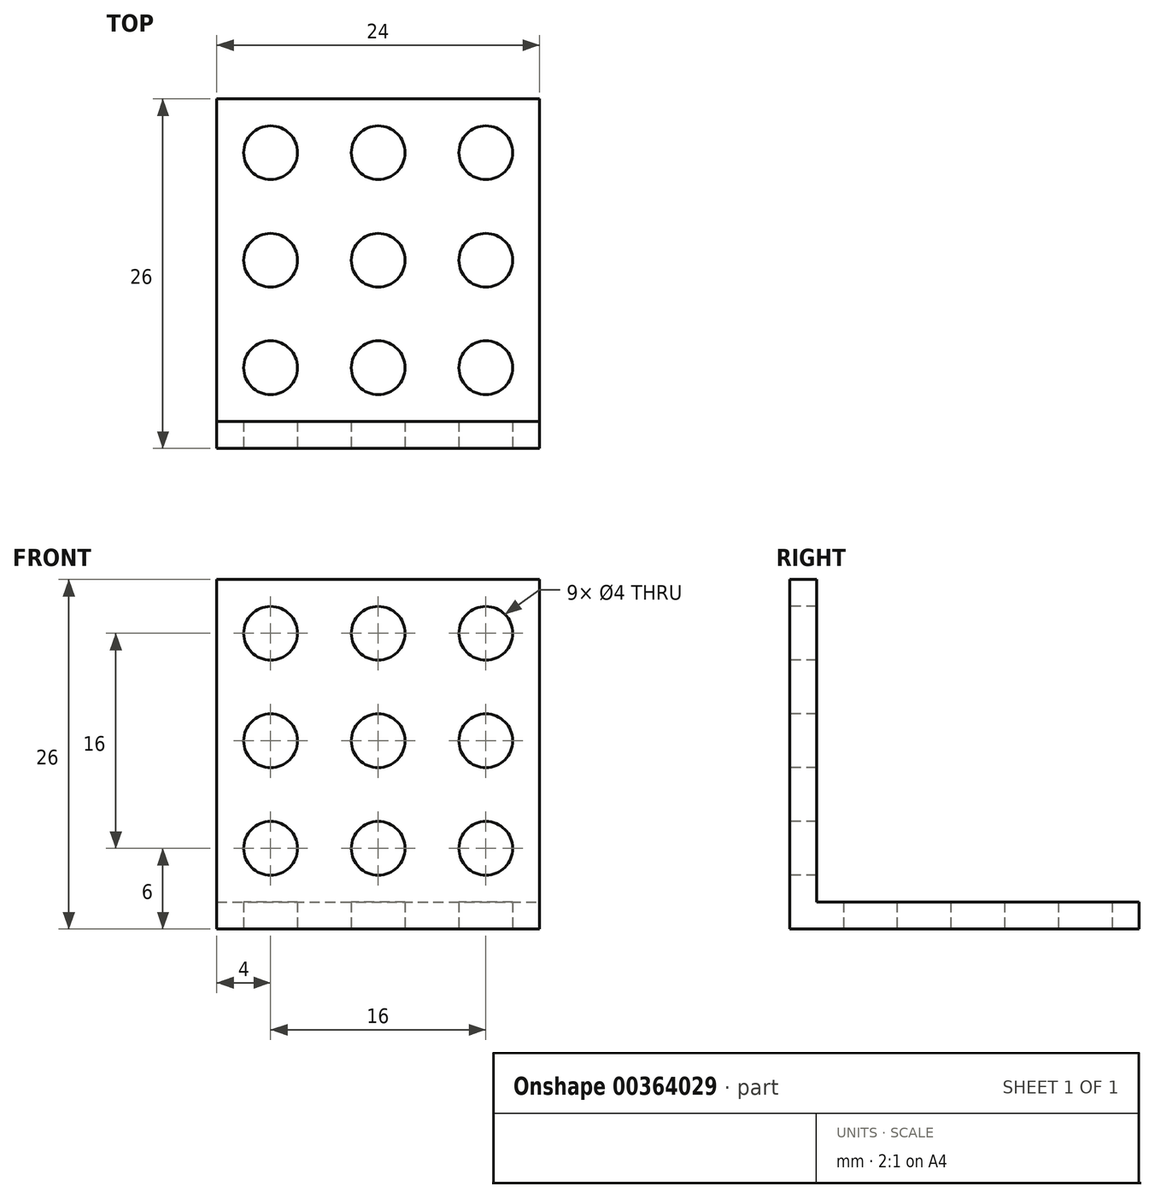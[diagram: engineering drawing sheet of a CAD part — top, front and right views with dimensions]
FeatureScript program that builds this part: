
annotation { "Feature Type Name" : "Feature", "Feature Type Description" : "" }
export const myFeature = defineFeature(function(context is Context, id is Id, definition is map)
    precondition{}
    {
        {
            var Q0;
            Q0=qCreatedBy(makeId("Top.planeOp"),FACE);
            var sketch = newSketch(context, id + "F0", { "sketchPlane" : qUnion([Q0])});
            skLineSegment(sketch, "E0", {"start": v(0, 0) * mm, "end": v(12, 0) * mm});
            skLineSegment(sketch, "E1", {"start": v(12, 0) * mm, "end": v(12, -26) * mm});
            skLineSegment(sketch, "E2", {"start": v(12, -26) * mm, "end": v(-12, -26) * mm});
            skLineSegment(sketch, "E3", {"start": v(-12, -26) * mm, "end": v(-12, 0) * mm});
            skLineSegment(sketch, "E4", {"start": v(-12, 0) * mm, "end": v(0, 0) * mm});
            skLineSegment(sketch, "E5", {"start": v(-12, -4) * mm, "end": v(-8, -4) * mm, "construction": true});
            skCircle(sketch, "E6", {"center": v(-8, -4) * mm, "radius": 2 * mm});
            skCircle(sketch, "E7.0.1.0", {"center": v(-8, -12) * mm, "radius": 2 * mm});
            skCircle(sketch, "E7.0.2.0", {"center": v(-8, -20) * mm, "radius": 2 * mm});
            skCircle(sketch, "E7.1.0.0", {"center": v(0, -4) * mm, "radius": 2 * mm});
            skCircle(sketch, "E7.1.1.0", {"center": v(0, -12) * mm, "radius": 2 * mm});
            skCircle(sketch, "E7.1.2.0", {"center": v(0, -20) * mm, "radius": 2 * mm});
            skCircle(sketch, "E7.2.0.0", {"center": v(8, -4) * mm, "radius": 2 * mm});
            skCircle(sketch, "E7.2.1.0", {"center": v(8, -12) * mm, "radius": 2 * mm});
            skCircle(sketch, "E7.2.2.0", {"center": v(8, -20) * mm, "radius": 2 * mm});
            skLineSegment(sketch, "E7.direction1", {"start": v(-8, -4) * mm, "end": v(0, -4) * mm, "construction": true});
            skLineSegment(sketch, "E7.direction2", {"start": v(-8, -4) * mm, "end": v(-8, -12) * mm, "construction": true});
            skSolve(sketch);
        }
        {
            var Q0;
            Q0 = qSketchRegion(id + "F0", true);
            extrude(context, id + "F1", {"entities" : qUnion([Q0]), "depth" : 2 * mm});
        }
        {
            var Q0;
            Q0=makeQuery(id+"F1.opExtrude","CAP_FACE",FACE,{"disambiguationData":[OSD([sQuery(id+"F0.wireOp",EDGE,"E0"),sQuery(id+"F0.wireOp",EDGE,"E1"),sQuery(id+"F0.wireOp",EDGE,"E2"),sQuery(id+"F0.wireOp",EDGE,"E3"),sQuery(id+"F0.wireOp",EDGE,"E4"),sQuery(id+"F0.wireOp",EDGE,"E6"),sQuery(id+"F0.wireOp",EDGE,"E7.0.1.0"),sQuery(id+"F0.wireOp",EDGE,"E7.0.2.0"),sQuery(id+"F0.wireOp",EDGE,"E7.1.0.0"),sQuery(id+"F0.wireOp",EDGE,"E7.1.1.0"),sQuery(id+"F0.wireOp",EDGE,"E7.1.2.0"),sQuery(id+"F0.wireOp",EDGE,"E7.2.0.0"),sQuery(id+"F0.wireOp",EDGE,"E7.2.1.0"),sQuery(id+"F0.wireOp",EDGE,"E7.2.2.0")])],"isStart":false});
            var sketch = newSketch(context, id + "F2", { "sketchPlane" : qUnion([Q0])});
            skLineSegment(sketch, "E8.bottom", {"start": v(-12, -26) * mm, "end": v(12, -26) * mm});
            skLineSegment(sketch, "E8.top", {"start": v(-12, -24) * mm, "end": v(12, -24) * mm});
            skLineSegment(sketch, "E8.left", {"start": v(-12, -26) * mm, "end": v(-12, -24) * mm});
            skLineSegment(sketch, "E8.right", {"start": v(12, -26) * mm, "end": v(12, -24) * mm});
            skSolve(sketch);
        }
        {
            var Q0;
            Q0 = qSketchRegion(id + "F2", true);
            extrude(context, id + "F3", {"entities" : qUnion([Q0]), "operationType" : NewBodyOperationType.ADD, "depth" : 24 * mm});
        }
        {
            var Q0;
            Q0=makeQuery(id+"F3.boolean.opBoolean","MERGE",FACE,{"derivedFrom":[makeQuery(id+"F1.opExtrude","SWEPT_FACE",FACE,{"disambiguationData":[OSD([sQuery(id+"F0.wireOp",EDGE,"E2")])]}),makeQuery(id+"F3.opExtrude","SWEPT_FACE",FACE,{"disambiguationData":[OSD([sQuery(id+"F2.wireOp",EDGE,"E8.bottom")])]})]});
            var sketch = newSketch(context, id + "F4", { "sketchPlane" : qUnion([Q0])});
            skLineSegment(sketch, "E9", {"start": v(-12, 22) * mm, "end": v(-8, 22) * mm, "construction": true});
            skCircle(sketch, "E10", {"center": v(-8, 22) * mm, "radius": 2 * mm});
            skCircle(sketch, "E11.0.1.0", {"center": v(-8, 14) * mm, "radius": 2 * mm});
            skCircle(sketch, "E11.0.2.0", {"center": v(-8, 6) * mm, "radius": 2 * mm});
            skCircle(sketch, "E11.1.0.0", {"center": v(0, 22) * mm, "radius": 2 * mm});
            skCircle(sketch, "E11.1.1.0", {"center": v(0, 14) * mm, "radius": 2 * mm});
            skCircle(sketch, "E11.1.2.0", {"center": v(0, 6) * mm, "radius": 2 * mm});
            skCircle(sketch, "E11.2.0.0", {"center": v(8, 22) * mm, "radius": 2 * mm});
            skCircle(sketch, "E11.2.1.0", {"center": v(8, 14) * mm, "radius": 2 * mm});
            skCircle(sketch, "E11.2.2.0", {"center": v(8, 6) * mm, "radius": 2 * mm});
            skLineSegment(sketch, "E11.direction1", {"start": v(-8, 22) * mm, "end": v(0, 22) * mm, "construction": true});
            skLineSegment(sketch, "E11.direction2", {"start": v(-8, 22) * mm, "end": v(-8, 14) * mm, "construction": true});
            skSolve(sketch);
        }
        {
            var Q0;
            Q0 = qSketchRegion(id + "F4", true);
            extrude(context, id + "F5", {"entities" : qUnion([Q0]), "operationType" : NewBodyOperationType.REMOVE, "oppositeDirection" : true, "depth" : 25 * mm});
        }
    });
